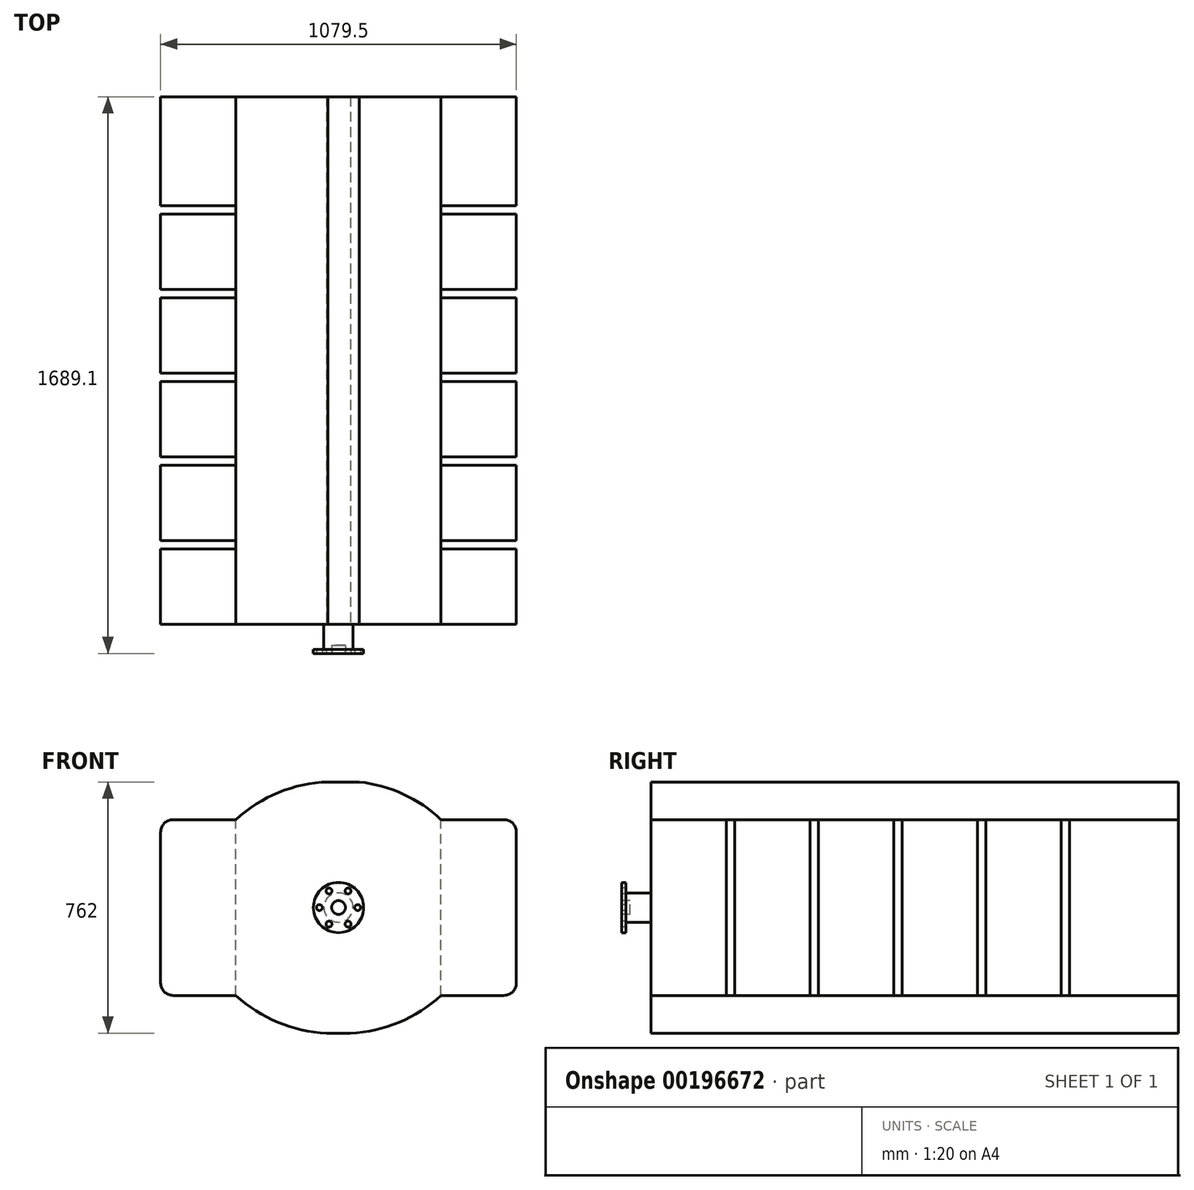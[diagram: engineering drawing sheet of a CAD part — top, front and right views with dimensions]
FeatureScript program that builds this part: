
annotation { "Feature Type Name" : "Feature", "Feature Type Description" : "" }
export const myFeature = defineFeature(function(context is Context, id is Id, definition is map)
    precondition{}
    {
        {
            var Q0;
            Q0=qCreatedBy(makeId("Front.planeOp"),FACE);
            var sketch = newSketch(context, id + "F0", { "sketchPlane" : qUnion([Q0])});
            skLineSegment(sketch, "E0.bottom", {"start": v(-539.75, 381) * mm, "end": v(539.75, 381) * mm});
            skLineSegment(sketch, "E0.top", {"start": v(-539.75, -381) * mm, "end": v(539.75, -381) * mm});
            skLineSegment(sketch, "E0.left", {"start": v(-539.75, 381) * mm, "end": v(-539.75, -381) * mm});
            skLineSegment(sketch, "E0.right", {"start": v(539.75, 381) * mm, "end": v(539.75, -381) * mm});
            skSolve(sketch);
        }
        {
            var Q0;
            Q0=makeQuery(id+"F0.imprint","IMPRINT",FACE,{"disambiguationData":[TD([[makeQuery(id+"F0.imprint","IMPRINT",EDGE,{"derivedFrom":sQuery(id+"F0.wireOp",EDGE,"E0.bottom")}),-1.0]])]});
            extrude(context, id + "F1", {"entities" : qUnion([Q0]), "depth" : 1600.2 * mm});
        }
        {
            var Q0;
            Q0=makeQuery(id+"F1.opExtrude","CAP_FACE",FACE,{"disambiguationData":[OSD([sQuery(id+"F0.wireOp",EDGE,"E0.bottom"),sQuery(id+"F0.wireOp",EDGE,"E0.top"),sQuery(id+"F0.wireOp",EDGE,"E0.left"),sQuery(id+"F0.wireOp",EDGE,"E0.right")])],"isStart":false});
            var sketch = newSketch(context, id + "F2", { "sketchPlane" : qUnion([Q0])});
            skLineSegment(sketch, "E1.top", {"start": v(-539.75, 152.4) * mm, "end": v(-311.15, 152.4) * mm});
            skLineSegment(sketch, "E1.left", {"start": v(-539.75, 266.7) * mm, "end": v(-539.75, 152.4) * mm});
            skLineSegment(sketch, "E1.right", {"start": v(-311.15, 266.7) * mm, "end": v(-311.15, 152.4) * mm});
            skLineSegment(sketch, "E2.top", {"start": v(-539.75, -152.4) * mm, "end": v(-311.15, -152.4) * mm});
            skLineSegment(sketch, "E2.left", {"start": v(-539.75, -266.7) * mm, "end": v(-539.75, -152.4) * mm});
            skLineSegment(sketch, "E2.right", {"start": v(-311.15, -266.7) * mm, "end": v(-311.15, -152.4) * mm});
            skLineSegment(sketch, "E3.top", {"start": v(539.75, -152.4) * mm, "end": v(311.15, -152.4) * mm});
            skLineSegment(sketch, "E3.left", {"start": v(539.75, -266.7) * mm, "end": v(539.75, -152.4) * mm});
            skLineSegment(sketch, "E3.right", {"start": v(311.15, -266.7) * mm, "end": v(311.15, -152.4) * mm});
            skLineSegment(sketch, "E4.top", {"start": v(539.75, 152.4) * mm, "end": v(311.15, 152.4) * mm});
            skLineSegment(sketch, "E4.left", {"start": v(539.75, 266.7) * mm, "end": v(539.75, 152.4) * mm});
            skLineSegment(sketch, "E4.right", {"start": v(311.15, 266.7) * mm, "end": v(311.15, 152.4) * mm});
            skArc(sketch, "E5", {"start": v(-31.87, 381) * mm, "mid": v(-181.82, 349.04) * mm, "end": v(-311.15, 266.7) * mm});
            skArc(sketch, "E6", {"start": v(311.15, 266.7) * mm, "mid": v(152.18, 361.48) * mm, "end": v(-31.87, 381) * mm});
            skPoint(sketch, "E1.bottom.end.orphan", {"position": v(-311.15, 381) * mm});
            skLineSegment(sketch, "E7", {"start": v(-311.15, 266.7) * mm, "end": v(-539.75, 266.7) * mm});
            skPoint(sketch, "E8.orphan", {"position": v(-539.75, 381) * mm});
            skPoint(sketch, "E4.bottom.end.orphan", {"position": v(311.15, 381) * mm});
            skLineSegment(sketch, "E9", {"start": v(311.15, 266.7) * mm, "end": v(539.75, 266.7) * mm});
            skPoint(sketch, "E10.orphan", {"position": v(539.75, 381) * mm});
            skArc(sketch, "E11", {"start": v(-311.15, -266.7) * mm, "mid": v(-166.98, -354.9) * mm, "end": v(0, -381) * mm});
            skArc(sketch, "E12", {"start": v(0, -381) * mm, "mid": v(166.98, -354.9) * mm, "end": v(311.15, -266.7) * mm});
            skPoint(sketch, "E13.orphan", {"position": v(-311.15, -381) * mm});
            skPoint(sketch, "E14.orphan", {"position": v(311.15, -381) * mm});
            skLineSegment(sketch, "E15", {"start": v(-311.15, -266.7) * mm, "end": v(-539.75, -266.7) * mm});
            skLineSegment(sketch, "E16", {"start": v(311.15, -266.7) * mm, "end": v(539.75, -266.7) * mm});
            skPoint(sketch, "E17.orphan", {"position": v(539.75, -381) * mm});
            skPoint(sketch, "E18.orphan", {"position": v(-539.75, -381) * mm});
            skSolve(sketch);
        }
        {
            var Q0;
            {var subQ0=sQuery(id+"F2.wireOp",EDGE,"E5");Q0=makeQuery(id+"F2.imprint","IMPRINT",FACE,{"disambiguationData":[TD([[makeQuery(id+"F2.imprint","IMPRINT",EDGE,{"derivedFrom":subQ0}),-1.0]])]});}
            var Q1;
            {var subQ0=sQuery(id+"F2.wireOp",EDGE,"E9");Q1=makeQuery(id+"F2.imprint","IMPRINT",FACE,{"disambiguationData":[TD([[makeQuery(id+"F2.imprint","IMPRINT",EDGE,{"derivedFrom":subQ0}),1.0]])]});}
            var Q2;
            {var subQ0=sQuery(id+"F2.wireOp",EDGE,"E16");Q2=makeQuery(id+"F2.imprint","IMPRINT",FACE,{"disambiguationData":[TD([[makeQuery(id+"F2.imprint","IMPRINT",EDGE,{"derivedFrom":subQ0}),-1.0]])]});}
            var Q3;
            {var subQ0=sQuery(id+"F2.wireOp",EDGE,"E15");Q3=makeQuery(id+"F2.imprint","IMPRINT",FACE,{"disambiguationData":[TD([[makeQuery(id+"F2.imprint","IMPRINT",EDGE,{"derivedFrom":subQ0}),1.0]])]});}
            extrude(context, id + "F3", {"entities" : qUnion([Q0, Q1, Q2, Q3]), "operationType" : NewBodyOperationType.REMOVE, "oppositeDirection" : true, "depth" : 2032 * mm});
        }
        {
            var Q0;
            Q0=makeQuery(id+"F3.boolean.opBoolean","COPY",FACE,{"derivedFrom":makeQuery(id+"F3.opExtrude","SWEPT_FACE",FACE,{"disambiguationData":[OSD([sQuery(id+"F2.wireOp",EDGE,"E7")])]})});
            var sketch = newSketch(context, id + "F4", { "sketchPlane" : qUnion([Q0])});
            skLineSegment(sketch, "E19.bottom", {"start": v(-539.75, -1371.6) * mm, "end": v(-311.15, -1371.6) * mm});
            skLineSegment(sketch, "E19.top", {"start": v(-539.75, -1346.2) * mm, "end": v(-311.15, -1346.2) * mm});
            skLineSegment(sketch, "E19.left", {"start": v(-539.75, -1371.6) * mm, "end": v(-539.75, -1346.2) * mm});
            skLineSegment(sketch, "E19.right", {"start": v(-311.15, -1371.6) * mm, "end": v(-311.15, -1346.2) * mm});
            skLineSegment(sketch, "E20.bottom", {"start": v(-539.75, -1117.6) * mm, "end": v(-311.15, -1117.6) * mm});
            skLineSegment(sketch, "E20.top", {"start": v(-539.75, -1092.2) * mm, "end": v(-311.15, -1092.2) * mm});
            skLineSegment(sketch, "E20.left", {"start": v(-539.75, -1117.6) * mm, "end": v(-539.75, -1092.2) * mm});
            skLineSegment(sketch, "E20.right", {"start": v(-311.15, -1117.6) * mm, "end": v(-311.15, -1092.2) * mm});
            skLineSegment(sketch, "E21.bottom", {"start": v(-539.75, -863.6) * mm, "end": v(-311.15, -863.6) * mm});
            skLineSegment(sketch, "E21.top", {"start": v(-539.75, -838.2) * mm, "end": v(-311.15, -838.2) * mm});
            skLineSegment(sketch, "E21.left", {"start": v(-539.75, -863.6) * mm, "end": v(-539.75, -838.2) * mm});
            skLineSegment(sketch, "E21.right", {"start": v(-311.15, -863.6) * mm, "end": v(-311.15, -838.2) * mm});
            skLineSegment(sketch, "E22.bottom", {"start": v(-539.75, -609.6) * mm, "end": v(-311.15, -609.6) * mm});
            skLineSegment(sketch, "E22.top", {"start": v(-539.75, -584.2) * mm, "end": v(-311.15, -584.2) * mm});
            skLineSegment(sketch, "E22.left", {"start": v(-539.75, -609.6) * mm, "end": v(-539.75, -584.2) * mm});
            skLineSegment(sketch, "E22.right", {"start": v(-311.15, -609.6) * mm, "end": v(-311.15, -584.2) * mm});
            skLineSegment(sketch, "E23.bottom", {"start": v(-311.15, -330.2) * mm, "end": v(-539.75, -330.2) * mm});
            skLineSegment(sketch, "E23.top", {"start": v(-311.15, -355.6) * mm, "end": v(-539.75, -355.6) * mm});
            skLineSegment(sketch, "E23.left", {"start": v(-311.15, -330.2) * mm, "end": v(-311.15, -355.6) * mm});
            skLineSegment(sketch, "E23.right", {"start": v(-539.75, -330.2) * mm, "end": v(-539.75, -355.6) * mm});
            skSolve(sketch);
        }
        {
            var Q0;
            Q0=makeQuery(id+"F4.imprint","IMPRINT",FACE,{"disambiguationData":[TD([[makeQuery(id+"F4.imprint","IMPRINT",EDGE,{"derivedFrom":sQuery(id+"F4.wireOp",EDGE,"E19.bottom")}),1.0]])]});
            var Q1;
            Q1=makeQuery(id+"F4.imprint","IMPRINT",FACE,{"disambiguationData":[TD([[makeQuery(id+"F4.imprint","IMPRINT",EDGE,{"derivedFrom":sQuery(id+"F4.wireOp",EDGE,"E20.bottom")}),1.0]])]});
            var Q2;
            Q2=makeQuery(id+"F4.imprint","IMPRINT",FACE,{"disambiguationData":[TD([[makeQuery(id+"F4.imprint","IMPRINT",EDGE,{"derivedFrom":sQuery(id+"F4.wireOp",EDGE,"E21.bottom")}),1.0]])]});
            var Q3;
            Q3=makeQuery(id+"F4.imprint","IMPRINT",FACE,{"disambiguationData":[TD([[makeQuery(id+"F4.imprint","IMPRINT",EDGE,{"derivedFrom":sQuery(id+"F4.wireOp",EDGE,"E22.bottom")}),1.0]])]});
            var Q4;
            Q4=makeQuery(id+"F4.imprint","IMPRINT",FACE,{"disambiguationData":[TD([[makeQuery(id+"F4.imprint","IMPRINT",EDGE,{"derivedFrom":sQuery(id+"F4.wireOp",EDGE,"E23.bottom")}),1.0]])]});
            extrude(context, id + "F5", {"entities" : qUnion([Q0, Q1, Q2, Q3, Q4]), "operationType" : NewBodyOperationType.REMOVE, "oppositeDirection" : true, "depth" : 889 * mm});
        }
        {
            var Q0;
            Q0=makeQuery(id+"F3.boolean.opBoolean","COPY",FACE,{"derivedFrom":makeQuery(id+"F3.opExtrude","SWEPT_FACE",FACE,{"disambiguationData":[OSD([sQuery(id+"F2.wireOp",EDGE,"E9")])]})});
            var sketch = newSketch(context, id + "F6", { "sketchPlane" : qUnion([Q0])});
            skLineSegment(sketch, "E24.bottom", {"start": v(311.15, -1371.6) * mm, "end": v(539.75, -1371.6) * mm});
            skLineSegment(sketch, "E24.top", {"start": v(311.15, -1346.2) * mm, "end": v(539.75, -1346.2) * mm});
            skLineSegment(sketch, "E24.left", {"start": v(311.15, -1371.6) * mm, "end": v(311.15, -1346.2) * mm});
            skLineSegment(sketch, "E24.right", {"start": v(539.75, -1371.6) * mm, "end": v(539.75, -1346.2) * mm});
            skLineSegment(sketch, "E25.bottom", {"start": v(311.15, -1117.6) * mm, "end": v(539.75, -1117.6) * mm});
            skLineSegment(sketch, "E25.top", {"start": v(311.15, -1092.2) * mm, "end": v(539.75, -1092.2) * mm});
            skLineSegment(sketch, "E25.left", {"start": v(311.15, -1117.6) * mm, "end": v(311.15, -1092.2) * mm});
            skLineSegment(sketch, "E25.right", {"start": v(539.75, -1117.6) * mm, "end": v(539.75, -1092.2) * mm});
            skLineSegment(sketch, "E26.bottom", {"start": v(311.15, -863.6) * mm, "end": v(539.75, -863.6) * mm});
            skLineSegment(sketch, "E26.top", {"start": v(311.15, -838.2) * mm, "end": v(539.75, -838.2) * mm});
            skLineSegment(sketch, "E26.left", {"start": v(311.15, -863.6) * mm, "end": v(311.15, -838.2) * mm});
            skLineSegment(sketch, "E26.right", {"start": v(539.75, -863.6) * mm, "end": v(539.75, -838.2) * mm});
            skLineSegment(sketch, "E27.bottom", {"start": v(311.15, -609.6) * mm, "end": v(539.75, -609.6) * mm});
            skLineSegment(sketch, "E27.top", {"start": v(311.15, -584.2) * mm, "end": v(539.75, -584.2) * mm});
            skLineSegment(sketch, "E27.left", {"start": v(311.15, -609.6) * mm, "end": v(311.15, -584.2) * mm});
            skLineSegment(sketch, "E27.right", {"start": v(539.75, -609.6) * mm, "end": v(539.75, -584.2) * mm});
            skLineSegment(sketch, "E28.bottom", {"start": v(311.15, -355.6) * mm, "end": v(539.75, -355.6) * mm});
            skLineSegment(sketch, "E28.top", {"start": v(311.15, -330.2) * mm, "end": v(539.75, -330.2) * mm});
            skLineSegment(sketch, "E28.left", {"start": v(311.15, -355.6) * mm, "end": v(311.15, -330.2) * mm});
            skLineSegment(sketch, "E28.right", {"start": v(539.75, -355.6) * mm, "end": v(539.75, -330.2) * mm});
            skSolve(sketch);
        }
        {
            var Q0;
            Q0=makeQuery(id+"F6.imprint","IMPRINT",FACE,{"disambiguationData":[TD([[makeQuery(id+"F6.imprint","IMPRINT",EDGE,{"derivedFrom":sQuery(id+"F6.wireOp",EDGE,"E24.bottom")}),1.0]])]});
            var Q1;
            Q1=makeQuery(id+"F6.imprint","IMPRINT",FACE,{"disambiguationData":[TD([[makeQuery(id+"F6.imprint","IMPRINT",EDGE,{"derivedFrom":sQuery(id+"F6.wireOp",EDGE,"E25.bottom")}),1.0]])]});
            var Q2;
            Q2=makeQuery(id+"F6.imprint","IMPRINT",FACE,{"disambiguationData":[TD([[makeQuery(id+"F6.imprint","IMPRINT",EDGE,{"derivedFrom":sQuery(id+"F6.wireOp",EDGE,"E26.bottom")}),1.0]])]});
            var Q3;
            Q3=makeQuery(id+"F6.imprint","IMPRINT",FACE,{"disambiguationData":[TD([[makeQuery(id+"F6.imprint","IMPRINT",EDGE,{"derivedFrom":sQuery(id+"F6.wireOp",EDGE,"E27.bottom")}),1.0]])]});
            var Q4;
            Q4=makeQuery(id+"F6.imprint","IMPRINT",FACE,{"disambiguationData":[TD([[makeQuery(id+"F6.imprint","IMPRINT",EDGE,{"derivedFrom":sQuery(id+"F6.wireOp",EDGE,"E28.bottom")}),1.0]])]});
            extrude(context, id + "F7", {"entities" : qUnion([Q0, Q1, Q2, Q3, Q4]), "operationType" : NewBodyOperationType.REMOVE, "oppositeDirection" : true, "depth" : 762 * mm});
        }
        {
            var Q0;
            Q0=makeQuery(id+"F1.opExtrude","CAP_FACE",FACE,{"disambiguationData":[OSD([sQuery(id+"F0.wireOp",EDGE,"E0.bottom"),sQuery(id+"F0.wireOp",EDGE,"E0.top"),sQuery(id+"F0.wireOp",EDGE,"E0.left"),sQuery(id+"F0.wireOp",EDGE,"E0.right")])],"isStart":false});
            var sketch = newSketch(context, id + "F8", { "sketchPlane" : qUnion([Q0])});
            skPoint(sketch, "E29", {"position": v(-501.65, 228.6) * mm});
            skPoint(sketch, "E30", {"position": v(-501.65, -228.6) * mm});
            skPoint(sketch, "E31", {"position": v(501.65, 228.6) * mm});
            skPoint(sketch, "E32", {"position": v(501.65, -228.6) * mm});
            skArc(sketch, "E33", {"start": v(-501.65, 266.7) * mm, "mid": v(-528.6, 255.54) * mm, "end": v(-539.75, 228.6) * mm});
            skCircle(sketch, "E34", {"center": v(-501.65, -228.6) * mm, "radius": 38.1 * mm});
            skCircle(sketch, "E35", {"center": v(501.65, -228.6) * mm, "radius": 38.1 * mm});
            skCircle(sketch, "E36", {"center": v(501.65, 228.6) * mm, "radius": 38.1 * mm});
            skSolve(sketch);
        }
        {
            var Q0;
            {var subQ0=sQuery(id+"F8.wireOp",EDGE,"E33");Q0=makeQuery(id+"F8.imprint","IMPRINT",FACE,{"disambiguationData":[TD([[makeQuery(id+"F8.imprint","IMPRINT",EDGE,{"derivedFrom":subQ0}),-1.0]])]});}
            var Q1;
            {var subQ0=sQuery(id+"F8.wireOp",EDGE,"E34");var subQ1=makeQuery(id+"F3.boolean.opBoolean","COPY",EDGE,{"derivedFrom":makeQuery(id+"F3.opExtrude","CAP_EDGE",EDGE,{"disambiguationData":[OSD([sQuery(id+"F2.wireOp",EDGE,"E15")])],"isStart":true})});var subQ2=makeQuery(id+"F8.imprint","INTERSECT",VERTEX,{"derivedFrom":[subQ1,subQ0]});Q1=makeQuery(id+"F8.imprint","IMPRINT",FACE,{"disambiguationData":[TD([[makeQuery(id+"F8.imprint","IMPRINT",EDGE,{"disambiguationData":[TD([[subQ2,1.0]])],"derivedFrom":subQ0}),-1.0]])]});}
            var Q2;
            {var subQ0=sQuery(id+"F8.wireOp",EDGE,"E35");var subQ1=makeQuery(id+"F3.boolean.opBoolean","COPY",EDGE,{"derivedFrom":makeQuery(id+"F3.opExtrude","CAP_EDGE",EDGE,{"disambiguationData":[OSD([sQuery(id+"F2.wireOp",EDGE,"E16")])],"isStart":true})});var subQ2=makeQuery(id+"F8.imprint","INTERSECT",VERTEX,{"derivedFrom":[subQ1,subQ0]});Q2=makeQuery(id+"F8.imprint","IMPRINT",FACE,{"disambiguationData":[TD([[makeQuery(id+"F8.imprint","IMPRINT",EDGE,{"disambiguationData":[TD([[subQ2,-1.0]])],"derivedFrom":subQ0}),-1.0]])]});}
            var Q3;
            {var subQ0=sQuery(id+"F8.wireOp",EDGE,"E36");var subQ1=makeQuery(id+"F3.boolean.opBoolean","COPY",EDGE,{"derivedFrom":makeQuery(id+"F3.opExtrude","CAP_EDGE",EDGE,{"disambiguationData":[OSD([sQuery(id+"F2.wireOp",EDGE,"E9")])],"isStart":true})});var subQ2=makeQuery(id+"F8.imprint","INTERSECT",VERTEX,{"derivedFrom":[subQ1,subQ0]});Q3=makeQuery(id+"F8.imprint","IMPRINT",FACE,{"disambiguationData":[TD([[makeQuery(id+"F8.imprint","IMPRINT",EDGE,{"disambiguationData":[TD([[subQ2,1.0]])],"derivedFrom":subQ0}),-1.0]])]});}
            extrude(context, id + "F9", {"entities" : qUnion([Q0, Q1, Q2, Q3]), "operationType" : NewBodyOperationType.REMOVE, "oppositeDirection" : true, "depth" : 2032 * mm});
        }
        {
            var Q0;
            Q0=makeQuery(id+"F1.opExtrude","CAP_FACE",FACE,{"disambiguationData":[OSD([sQuery(id+"F0.wireOp",EDGE,"E0.bottom"),sQuery(id+"F0.wireOp",EDGE,"E0.top"),sQuery(id+"F0.wireOp",EDGE,"E0.left"),sQuery(id+"F0.wireOp",EDGE,"E0.right")])],"isStart":false});
            var sketch = newSketch(context, id + "F10", { "sketchPlane" : qUnion([Q0])});
            skCircle(sketch, "E37", {"center": v(0, 0) * mm, "radius": 44.45 * mm});
            skSolve(sketch);
        }
        {
            var Q0;
            Q0=makeQuery(id+"F10.imprint","IMPRINT",FACE,{"disambiguationData":[TD([[makeQuery(id+"F10.imprint","IMPRINT",EDGE,{"derivedFrom":sQuery(id+"F10.wireOp",EDGE,"E37")}),1.0]])]});
            extrude(context, id + "F11", {"entities" : qUnion([Q0]), "operationType" : NewBodyOperationType.ADD, "depth" : 76.2 * mm});
        }
        {
            var Q0;
            Q0=makeQuery(id+"F11.opExtrude","CAP_FACE",FACE,{"disambiguationData":[OSD([sQuery(id+"F10.wireOp",EDGE,"E37")])],"isStart":false});
            var sketch = newSketch(context, id + "F12", { "sketchPlane" : qUnion([Q0])});
            skCircle(sketch, "E38", {"center": v(0, 0) * mm, "radius": 76.2 * mm});
            skSolve(sketch);
        }
        {
            var Q0;
            Q0=makeQuery(id+"F12.imprint","IMPRINT",FACE,{"disambiguationData":[TD([[makeQuery(id+"F12.imprint","IMPRINT",EDGE,{"derivedFrom":makeQuery(id+"F11.opExtrude","CAP_EDGE",EDGE,{"disambiguationData":[OSD([sQuery(id+"F10.wireOp",EDGE,"E37")])],"isStart":false})}),1.0]])]});
            var Q1;
            Q1=makeQuery(id+"F12.imprint","IMPRINT",FACE,{"disambiguationData":[TD([[makeQuery(id+"F12.imprint","IMPRINT",EDGE,{"derivedFrom":sQuery(id+"F12.wireOp",EDGE,"E38")}),1.0]])]});
            extrude(context, id + "F13", {"entities" : qUnion([Q0, Q1]), "operationType" : NewBodyOperationType.ADD, "depth" : 12.7 * mm});
        }
        {
            var Q0;
            Q0=makeQuery(id+"F13.opExtrude","CAP_FACE",FACE,{"disambiguationData":[OSD([sQuery(id+"F12.wireOp",EDGE,"E38")])],"isStart":false});
            var sketch = newSketch(context, id + "F14", { "sketchPlane" : qUnion([Q0])});
            skCircle(sketch, "E39", {"center": v(0, 0) * mm, "radius": 20.88 * mm});
            skPoint(sketch, "E40", {"position": v(-57.99, 0) * mm});
            skPoint(sketch, "E41", {"position": v(57.99, 0) * mm});
            skPoint(sketch, "E42", {"position": v(29.03, -50.24) * mm});
            skPoint(sketch, "E43", {"position": v(-29, 50.22) * mm});
            skPoint(sketch, "E44", {"position": v(-29, -50.22) * mm});
            skPoint(sketch, "E45", {"position": v(29, 50.22) * mm});
            skCircle(sketch, "E46", {"center": v(-29, -50.22) * mm, "radius": 9 * mm});
            skCircle(sketch, "E47", {"center": v(-57.99, 0) * mm, "radius": 9 * mm});
            skCircle(sketch, "E48", {"center": v(-29, 50.22) * mm, "radius": 9 * mm});
            skCircle(sketch, "E49", {"center": v(29, 50.22) * mm, "radius": 9 * mm});
            skCircle(sketch, "E50", {"center": v(57.99, 0) * mm, "radius": 9 * mm});
            skCircle(sketch, "E51", {"center": v(29.03, -50.24) * mm, "radius": 9 * mm});
            skSolve(sketch);
        }
        {
            var Q0;
            Q0=makeQuery(id+"F14.imprint","IMPRINT",FACE,{"disambiguationData":[TD([[makeQuery(id+"F14.imprint","IMPRINT",EDGE,{"derivedFrom":sQuery(id+"F14.wireOp",EDGE,"E48")}),1.0]])]});
            var Q1;
            Q1=makeQuery(id+"F14.imprint","IMPRINT",FACE,{"disambiguationData":[TD([[makeQuery(id+"F14.imprint","IMPRINT",EDGE,{"derivedFrom":sQuery(id+"F14.wireOp",EDGE,"E47")}),1.0]])]});
            var Q2;
            Q2=makeQuery(id+"F14.imprint","IMPRINT",FACE,{"disambiguationData":[TD([[makeQuery(id+"F14.imprint","IMPRINT",EDGE,{"derivedFrom":sQuery(id+"F14.wireOp",EDGE,"E46")}),1.0]])]});
            var Q3;
            Q3=makeQuery(id+"F14.imprint","IMPRINT",FACE,{"disambiguationData":[TD([[makeQuery(id+"F14.imprint","IMPRINT",EDGE,{"derivedFrom":sQuery(id+"F14.wireOp",EDGE,"E51")}),1.0]])]});
            var Q4;
            Q4=makeQuery(id+"F14.imprint","IMPRINT",FACE,{"disambiguationData":[TD([[makeQuery(id+"F14.imprint","IMPRINT",EDGE,{"derivedFrom":sQuery(id+"F14.wireOp",EDGE,"E50")}),1.0]])]});
            var Q5;
            Q5=makeQuery(id+"F14.imprint","IMPRINT",FACE,{"disambiguationData":[TD([[makeQuery(id+"F14.imprint","IMPRINT",EDGE,{"derivedFrom":sQuery(id+"F14.wireOp",EDGE,"E49")}),1.0]])]});
            var Q6;
            Q6=makeQuery(id+"F14.imprint","IMPRINT",FACE,{"disambiguationData":[TD([[makeQuery(id+"F14.imprint","IMPRINT",EDGE,{"derivedFrom":sQuery(id+"F14.wireOp",EDGE,"E39")}),1.0]])]});
            extrude(context, id + "F15", {"entities" : qUnion([Q0, Q1, Q2, Q3, Q4, Q5, Q6]), "operationType" : NewBodyOperationType.REMOVE, "oppositeDirection" : true, "depth" : 25.4 * mm});
        }
    });
